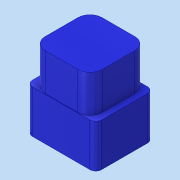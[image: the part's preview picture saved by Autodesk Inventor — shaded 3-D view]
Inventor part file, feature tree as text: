
AUTODESK INVENTOR PART (.ipt)
format: ipt  version: 2018 (Build 220112000, 112)  size: 144,384 bytes
history: native  units: mm
features: extrude x2, fillet x2, sketch x2
ambient origin geometry x8: Origin, YZ Plane, XZ Plane, XY Plane, X Axis, Y Axis, Z Axis, Center Point
bodies: Volumenkörper1 (feature_tree)
feature tree (6):
  extrude  "Extrusion1"  Depth=10.0mm
  extrude  "Extrusion2"  Depth=9.9mm
  fillet  "Rundung1"  Radius=9.9mm
  fillet  "Rundung2"  Radius=6.5mm
  sketch  "Skizze1"  dims[d0=12.0mm d1=10.0mm]
  sketch  "Skizze2"  dims[d2=14.0mm d3=0.0mm d4=9.9mm d5=9.9mm d6=6.5mm d7=0.0mm d8=2.1mm d9=1.0mm]
